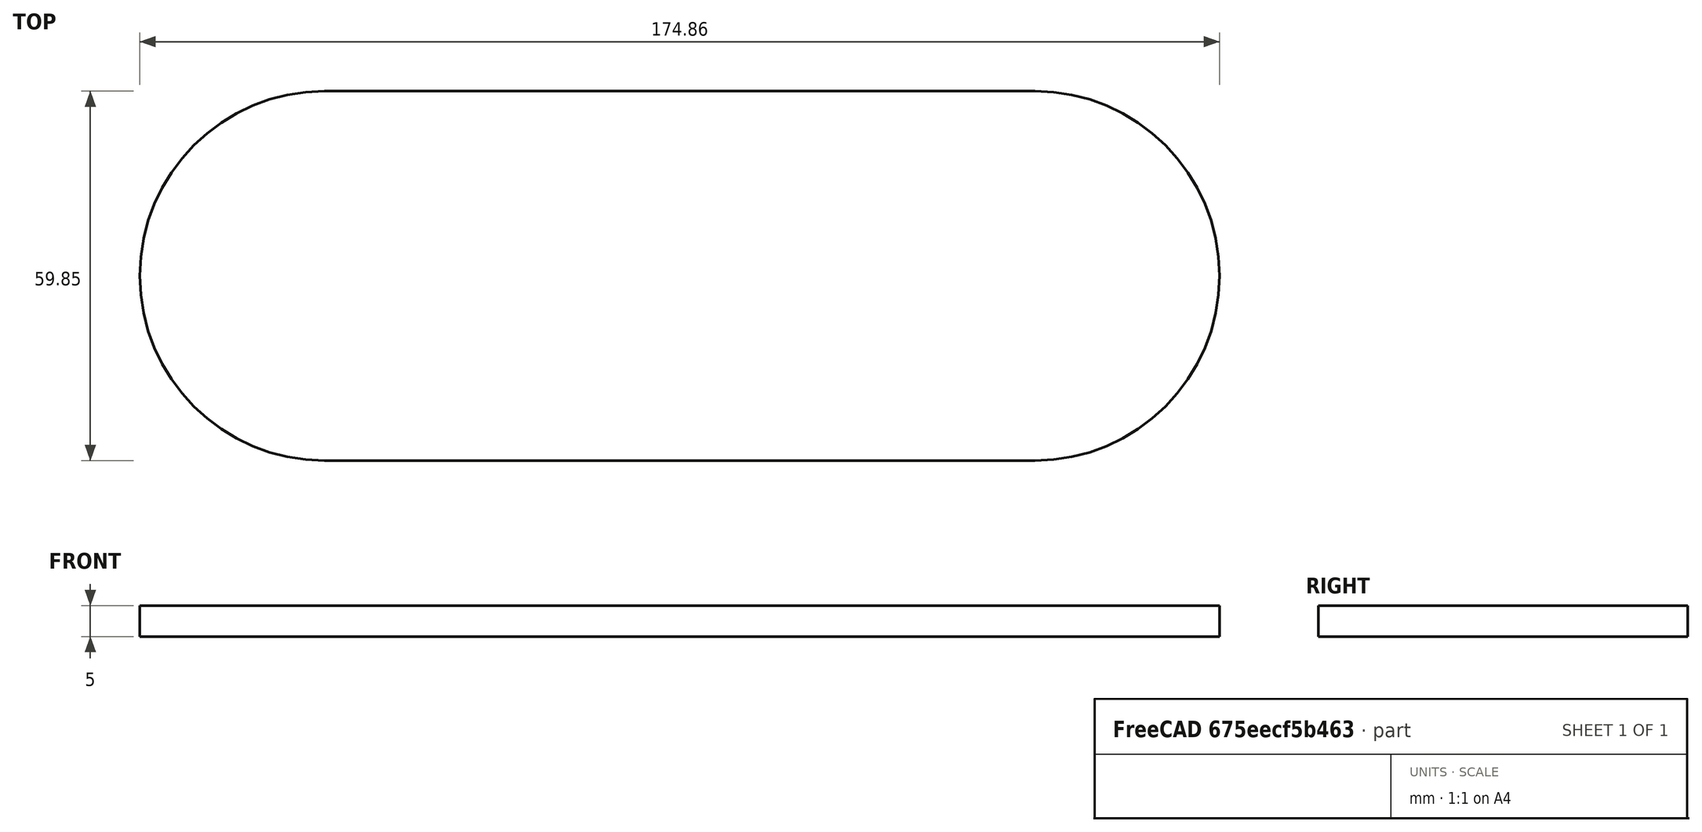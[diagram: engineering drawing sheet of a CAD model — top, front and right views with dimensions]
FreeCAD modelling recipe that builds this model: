
FCSTD DOCUMENT  (FreeCAD 0.18R4 (GitTag))
Label: jacuzziMainPanel
License: All rights reserved
LicenseURL: http://en.wikipedia.org/wiki/All_rights_reserved
objects: Sketcher::SketchObject×2, PartDesign::Pad×1, PartDesign::Body×1
note: 5 computed .brp shape members not serialized (recipe doc carries the construction recipe); baked Part::Feature solids carry a one-line shape summary decoded from their .brp

FEATURE [Sketcher::SketchObject] Sketch
  MapMode = 2
  Support = -> [Sketch]
  sketch-geometry (4):
    g0: ArcOfCircle CenterX=145 CenterY=29.9268 CenterZ=0 NormalX=0 NormalY=0 NormalZ=1 AngleXU=0 Radius=29.9268 StartAngle=4.71239 EndAngle=7.85398
    g1: ArcOfCircle CenterX=30 CenterY=29.9268 CenterZ=0 NormalX=0 NormalY=0 NormalZ=1 AngleXU=0 Radius=29.9268 StartAngle=1.5708 EndAngle=4.71239
    g2: LineSegment StartX=29.9999 StartY=59.8536 StartZ=0 EndX=145 EndY=59.8536 EndZ=0
    g3: LineSegment StartX=30 StartY=7.38147e-11 StartZ=0 EndX=145 EndY=7.38147e-11 EndZ=0
  constraints (7):
    c: Equal(g0,g1)
    c: Coincident(g2,g1)
    c: Coincident(g2,g0)
    c: Horizontal(g2)
    c: Coincident(g3,g1)
    c: Coincident(g3,g0)
    c: Horizontal(g3)
FEATURE [PartDesign::Pad] Pad
  Length = 5
  Length2 = 100
  Profile = -> Sketch
  Type = 0
FEATURE [Sketcher::SketchObject] Sketch001
  MapMode = 5
  Support = -> [XY_Plane]
FEATURE [PartDesign::Body] Body
  Group = -> [Sketch,Pad,Sketch001]
  Origin = -> Origin
  Tip = -> Pad
